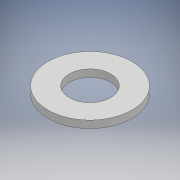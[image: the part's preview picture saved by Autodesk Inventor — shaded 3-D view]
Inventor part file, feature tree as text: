
AUTODESK INVENTOR PART (.ipt)
format: ipt  version: 2018 (Build 220112000, 112)  size: 96,256 bytes
history: native  units: mm
features: other x1, extrude x1, sketch x1
ambient origin geometry x8: Origin, YZ Plane, XZ Plane, XY Plane, X Axis, Y Axis, Z Axis, Center Point
bodies: Body1 (feature_tree)
feature tree (3):
  other  "ソリッド1"
  extrude  "押し出し1"  Depth=25.8mm
  sketch  "スケッチ1"
